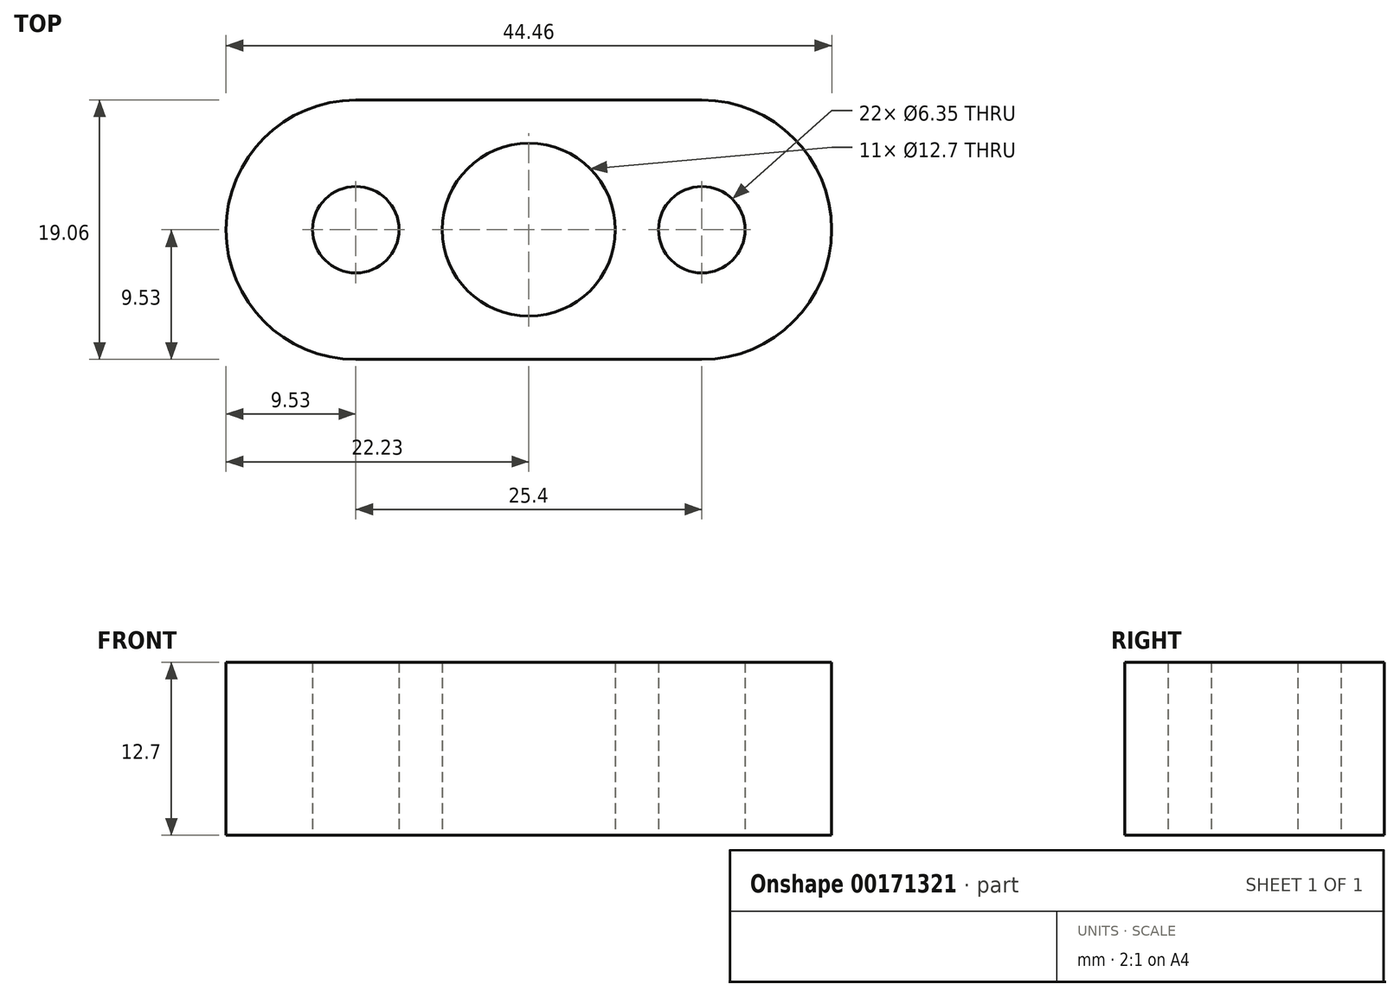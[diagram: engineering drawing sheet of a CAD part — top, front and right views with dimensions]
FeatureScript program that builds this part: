
annotation { "Feature Type Name" : "Feature", "Feature Type Description" : "" }
export const myFeature = defineFeature(function(context is Context, id is Id, definition is map)
    precondition{}
    {
        {
            var Q0;
            Q0=qCreatedBy(makeId("Top.planeOp"),FACE);
            var sketch = newSketch(context, id + "F0", { "sketchPlane" : qUnion([Q0])});
            skLineSegment(sketch, "E0.bottom", {"start": v(12.7, 9.53) * mm, "end": v(-12.7, 9.52) * mm});
            skLineSegment(sketch, "E0.top", {"start": v(12.7, -9.52) * mm, "end": v(-12.7, -9.53) * mm});
            skPoint(sketch, "E0.middle", {"position": v(0, 0) * mm});
            skArc(sketch, "E1", {"start": v(12.7, -9.52) * mm, "mid": v(22.23, 0) * mm, "end": v(12.7, 9.53) * mm});
            skArc(sketch, "E2", {"start": v(-12.7, 9.52) * mm, "mid": v(-22.23, 0) * mm, "end": v(-12.7, -9.53) * mm});
            skCircle(sketch, "E3", {"center": v(0, 0) * mm, "radius": 6.35 * mm});
            skCircle(sketch, "E4", {"center": v(-12.7, 0) * mm, "radius": 3.18 * mm});
            skCircle(sketch, "E5", {"center": v(12.7, 0) * mm, "radius": 3.18 * mm});
            skSolve(sketch);
        }
        {
            var Q0;
            Q0=makeQuery(id+"F0.imprint","IMPRINT",FACE,{"disambiguationData":[TD([[makeQuery(id+"F0.imprint","IMPRINT",EDGE,{"derivedFrom":sQuery(id+"F0.wireOp",EDGE,"E0.bottom")}),1.0]])]});
            extrude(context, id + "F1", {"entities" : qUnion([Q0]), "depth" : 12.7 * mm});
        }
    });
